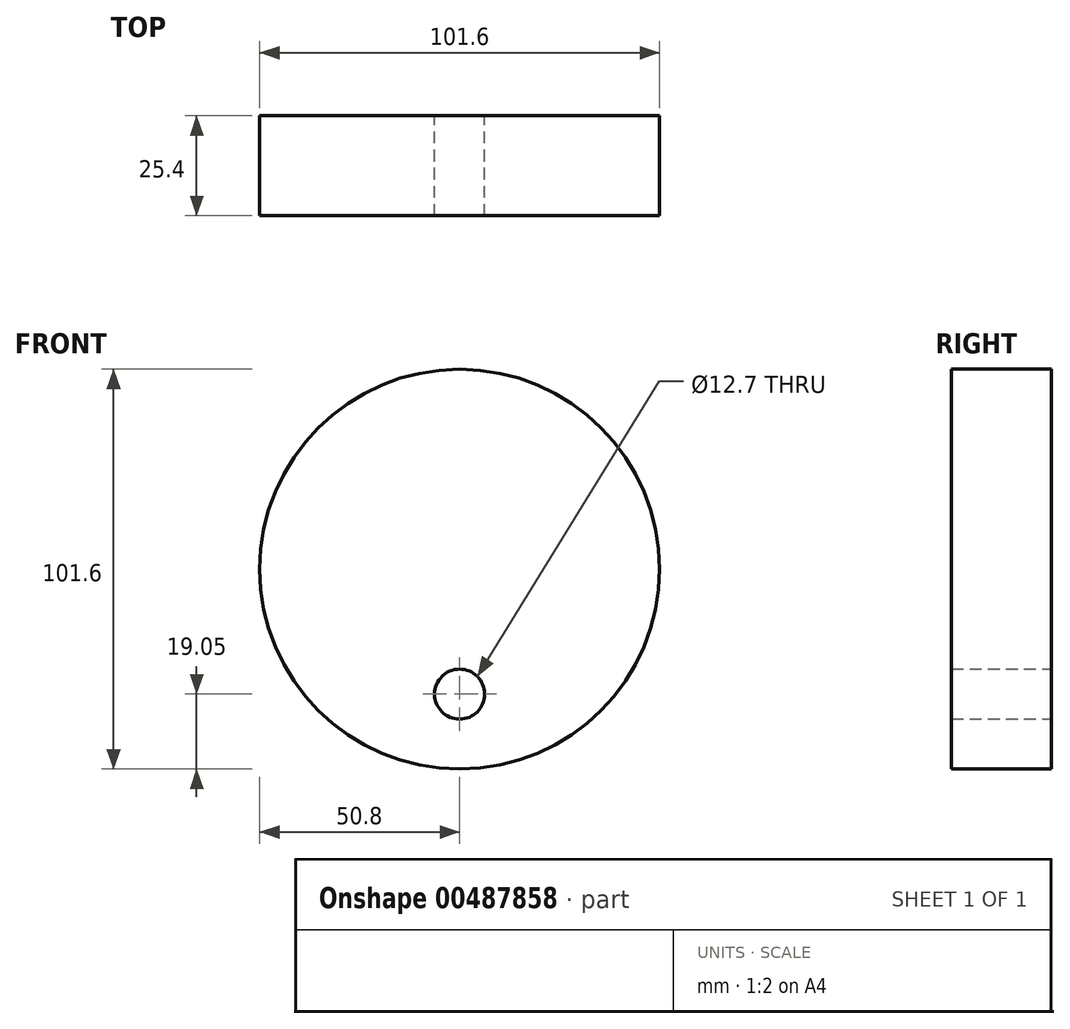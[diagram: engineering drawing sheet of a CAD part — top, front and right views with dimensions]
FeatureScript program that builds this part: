
annotation { "Feature Type Name" : "Feature", "Feature Type Description" : "" }
export const myFeature = defineFeature(function(context is Context, id is Id, definition is map)
    precondition{}
    {
        {
            var Q0;
            Q0=qCreatedBy(makeId("Front.planeOp"),FACE);
            var sketch = newSketch(context, id + "F0", { "sketchPlane" : qUnion([Q0])});
            skCircle(sketch, "E0", {"center": v(0, 0) * mm, "radius": 50.8 * mm});
            skSolve(sketch);
        }
        {
            var Q0;
            Q0 = qSketchRegion(id + "F0", true);
            extrude(context, id + "F1", {"entities" : qUnion([Q0]), "depth" : 25.4 * mm});
        }
        {
            var Q0;
            Q0=qCreatedBy(makeId("Front.planeOp"),FACE);
            var sketch = newSketch(context, id + "F2", { "sketchPlane" : qUnion([Q0])});
            skCircle(sketch, "E1", {"center": v(0, 0) * mm, "radius": 31.75 * mm, "construction": true});
            skCircle(sketch, "E2", {"center": v(0, -31.75) * mm, "radius": 6.35 * mm});
            skSolve(sketch);
        }
        {
            var Q0;
            Q0 = qSketchRegion(id + "F2", true);
            extrude(context, id + "F3", {"entities" : qUnion([Q0]), "operationType" : NewBodyOperationType.REMOVE, "endBound" : BoundingType.THROUGH_ALL, "depth" : 25.4 * mm});
        }
        {
            var Q0;
            Q0=qCreatedBy(makeId("Front.planeOp"),FACE);
            var sketch = newSketch(context, id + "F4", { "sketchPlane" : qUnion([Q0])});
            skCircle(sketch, "E3", {"center": v(0, 0) * mm, "radius": 31.75 * mm, "construction": true});
            skSolve(sketch);
        }
    });
